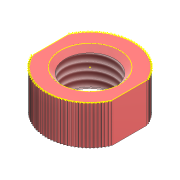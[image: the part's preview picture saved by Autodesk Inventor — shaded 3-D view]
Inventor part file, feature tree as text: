
AUTODESK INVENTOR PART (.ipt)
format: ipt  version: 2022.3 (Build 263350000, 350)  size: 493,056 bytes
history: native  units: mm
features: sketch x2, other x1, extrude x1, chamfer x1, thread x1, projected_geometry x1
ambient origin geometry x8: Origin, YZ Plane, XZ Plane, XY Plane, X Axis, Y Axis, Z Axis, Center Point
bodies: Body1 (feature_tree)
feature tree (7):
  other  "Sólido1"
  extrude  "Extrusión1"  Depth=8.0mm TaperAngle=0.0deg
  chamfer  "Chaflán1"  Distance=1.0mm Angle=45.0deg
  thread  "Rosca1"  [1 undecoded]
  sketch  "Boceto2"
  sketch  "Boceto1"  dims[d0=10.0mm d1=8.0mm d2=0.0mm d3=1.0mm d4=2.0mm d5=45.0deg d6=6.2mm d7=0.0mm]
  projected_geometry  "Contorno proyectado1"
note: 1 required parameter value undecoded (feature->parameter linkage not recoverable at this tier; creation-order binding heuristic only, values carry confidence <= 0.55)
